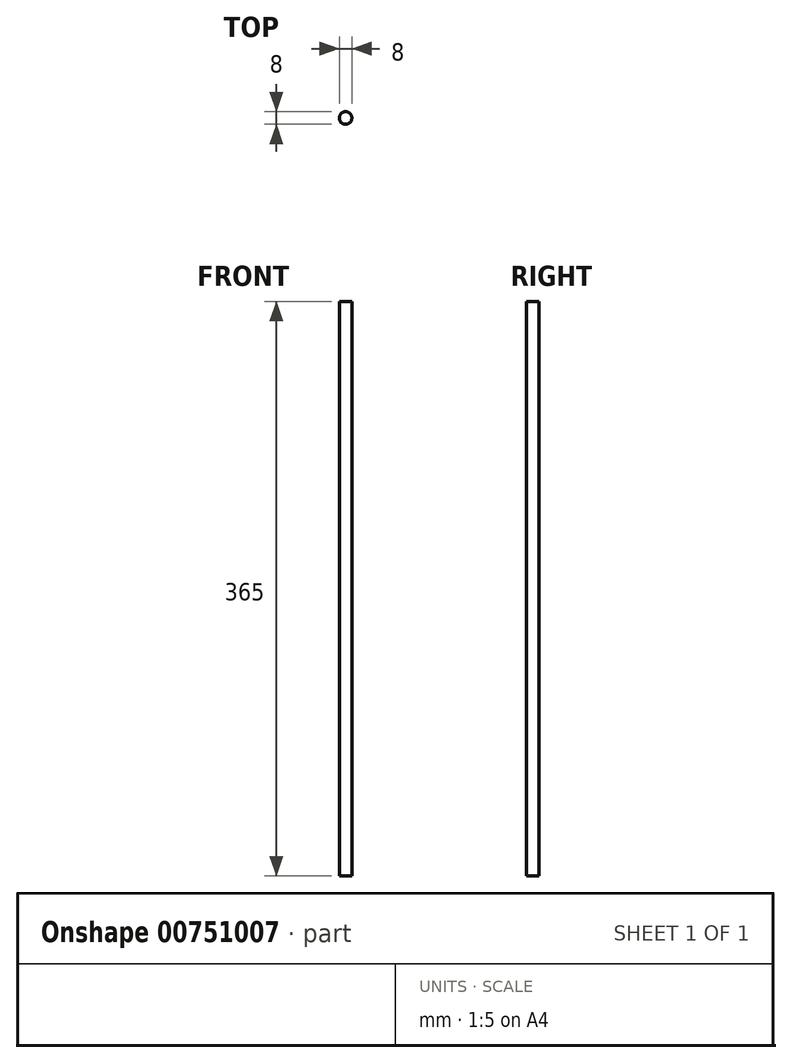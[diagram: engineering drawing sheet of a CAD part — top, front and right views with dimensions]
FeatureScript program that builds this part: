
annotation { "Feature Type Name" : "Feature", "Feature Type Description" : "" }
export const myFeature = defineFeature(function(context is Context, id is Id, definition is map)
    precondition{}
    {
        {
            var Q0;
            Q0=qCreatedBy(makeId("Top.planeOp"),FACE);
            var sketch = newSketch(context, id + "F0", { "sketchPlane" : qUnion([Q0])});
            skCircle(sketch, "E0", {"center": v(0, 0) * mm, "radius": 4 * mm});
            skSolve(sketch);
        }
        {
            var Q0;
            Q0=makeQuery(id+"F0.imprint","IMPRINT",FACE,{"disambiguationData":[TD([[makeQuery(id+"F0.imprint","IMPRINT",EDGE,{"derivedFrom":sQuery(id+"F0.wireOp",EDGE,"E0")}),1.0]])]});
            extrude(context, id + "F1", {"entities" : qUnion([Q0]), "endBound" : BoundingType.SYMMETRIC, "depth" : 365 * mm, "offsetDistance" : 25 * mm});
        }
    });
